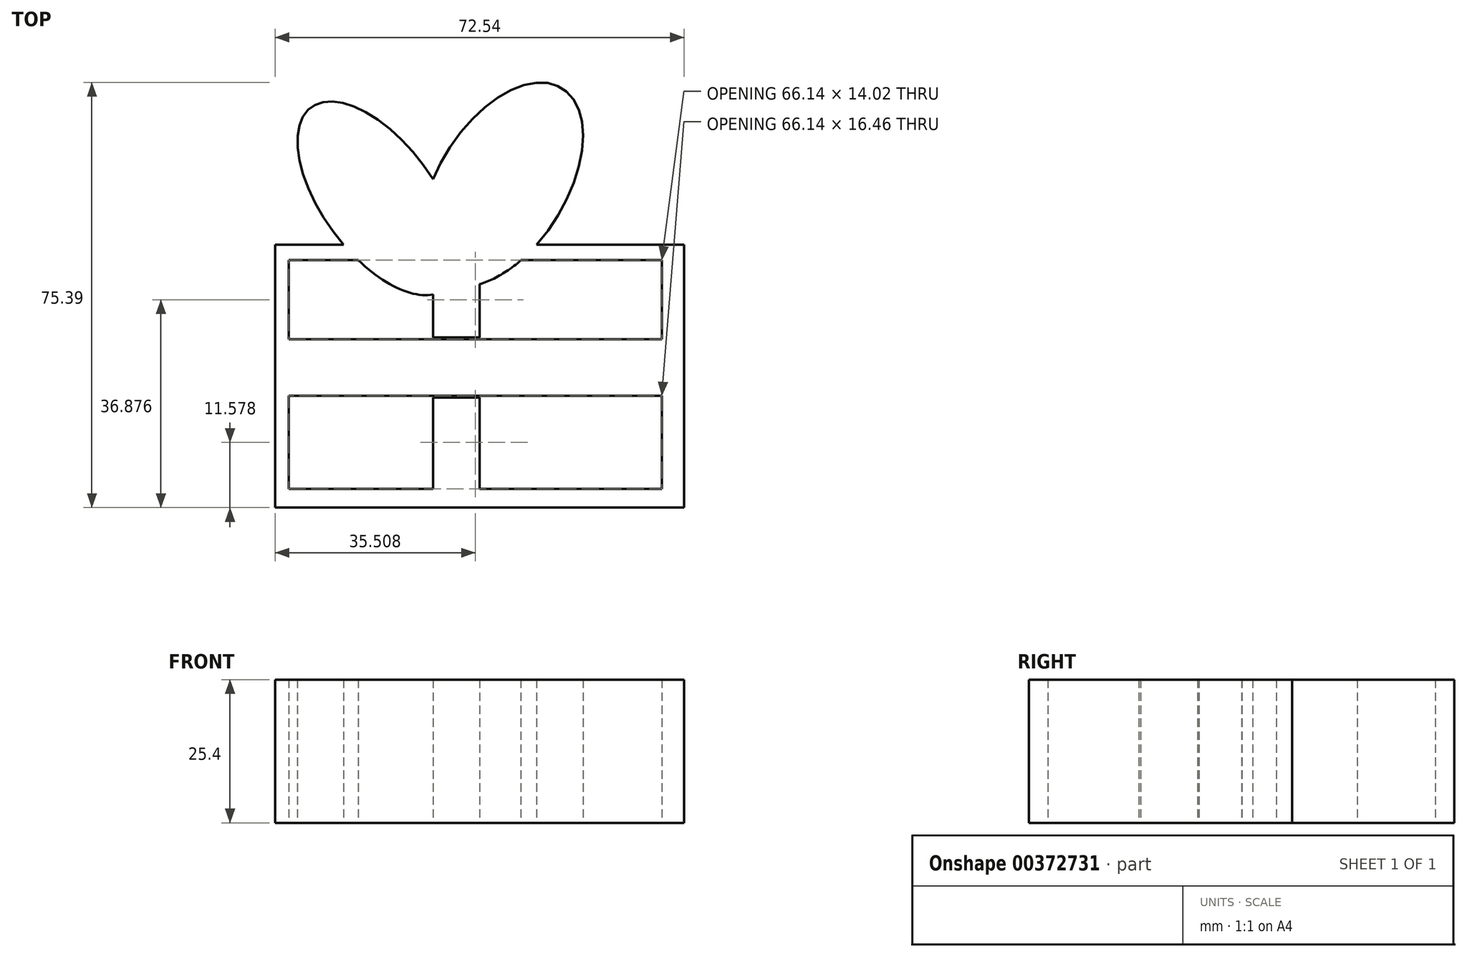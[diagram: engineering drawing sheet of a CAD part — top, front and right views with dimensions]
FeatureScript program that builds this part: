
annotation { "Feature Type Name" : "Feature", "Feature Type Description" : "" }
export const myFeature = defineFeature(function(context is Context, id is Id, definition is map)
    precondition{}
    {
        {
            var Q0;
            Q0=qCreatedBy(makeId("Top.planeOp"),FACE);
            var sketch = newSketch(context, id + "F0", { "sketchPlane" : qUnion([Q0])});
            skLineSegment(sketch, "E0.bottom", {"start": v(-28.04, 12.04) * mm, "end": v(44.5, 12.04) * mm});
            skLineSegment(sketch, "E0.top", {"start": v(-28.04, -34.6) * mm, "end": v(44.5, -34.6) * mm});
            skLineSegment(sketch, "E0.left", {"start": v(-28.04, 12.04) * mm, "end": v(-28.04, -34.6) * mm});
            skLineSegment(sketch, "E0.right", {"start": v(44.5, 12.04) * mm, "end": v(44.5, -34.6) * mm});
            skLineSegment(sketch, "E1.bottom", {"start": v(-25.6, 9.3) * mm, "end": v(40.54, 9.3) * mm});
            skLineSegment(sketch, "E1.top", {"start": v(-25.6, -31.24) * mm, "end": v(40.54, -31.24) * mm});
            skLineSegment(sketch, "E1.left", {"start": v(-25.6, 9.3) * mm, "end": v(-25.6, -31.24) * mm});
            skLineSegment(sketch, "E1.right", {"start": v(40.54, 9.3) * mm, "end": v(40.54, -31.24) * mm});
            skLineSegment(sketch, "E2.bottom", {"start": v(-25.6, -4.72) * mm, "end": v(44.5, -4.72) * mm});
            skLineSegment(sketch, "E2.top", {"start": v(-25.6, -4.42) * mm, "end": v(44.5, -4.42) * mm});
            skLineSegment(sketch, "E2.left", {"start": v(-28.04, -4.72) * mm, "end": v(-28.04, -4.42) * mm});
            skLineSegment(sketch, "E2.right", {"start": v(44.5, -4.72) * mm, "end": v(44.5, -4.42) * mm});
            skLineSegment(sketch, "E3.bottom", {"start": v(-25.6, -15.09) * mm, "end": v(44.5, -15.09) * mm});
            skLineSegment(sketch, "E3.top", {"start": v(-25.6, -14.78) * mm, "end": v(44.5, -14.78) * mm});
            skLineSegment(sketch, "E3.left", {"start": v(-25.6, -15.09) * mm, "end": v(-25.6, -14.78) * mm});
            skLineSegment(sketch, "E3.right", {"start": v(44.5, -15.09) * mm, "end": v(44.5, -14.78) * mm});
            skLineSegment(sketch, "E4", {"start": v(0, 9.3) * mm, "end": v(0, -31.24) * mm});
            skLineSegment(sketch, "E5", {"start": v(8.23, 9.3) * mm, "end": v(8.23, -31.24) * mm});
            skPoint(sketch, "E5.startSnap0", {"position": v(7.47, 9.3) * mm});
            skPoint(sketch, "E5.startSnap1", {"position": v(8.23, 12.04) * mm});
            skPoint(sketch, "E6.1.internal.orphan", {"position": v(0, 23.62) * mm});
            skEllipticalArc(sketch, "E7", {});
            skEllipticalArc(sketch, "E8.trimOffspring", {});
            const initialGuessF0  = {"E7": [-0.00975360069423914, 0.020269200205802917, 0.5926805994036081, -0.8054375873341025, 0.020056675187534876, 0.00993114980581942, 1.418696932754669, 0.12206321532883095], "E8.trimOffspring": [0.012191999703645706, 0.02270760014653206, -0.5299989795139679, -0.8479982793108444, 0.0201283427893708, 0.011335019917126201, 0.14448277518461064, 4.9992793105523]};
            skSetInitialGuess(sketch, initialGuessF0);
            skSolve(sketch);
        }
        {
            var Q0;
            Q0 = qSketchRegion(id + "F0", true);
            var Q1;
            {var subQ0=sQuery(id+"F0.wireOp",EDGE,"E2.bottom");var subQ1=sQuery(id+"F0.wireOp",EDGE,"E1.left");var subQ2=makeQuery(id+"F0.imprint","INTERSECT",VERTEX,{"derivedFrom":[subQ1,subQ0]});Q1=makeQuery(id+"F0.imprint","IMPRINT",FACE,{"disambiguationData":[TD([[makeQuery(id+"F0.imprint","IMPRINT",EDGE,{"disambiguationData":[TD([[subQ2,-1.0]])],"derivedFrom":subQ0}),-1.0]])]});}
            var Q2;
            {var subQ0=sQuery(id+"F0.wireOp",EDGE,"E4");var subQ1=sQuery(id+"F0.wireOp",EDGE,"E2.bottom");var subQ2=makeQuery(id+"F0.imprint","INTERSECT",VERTEX,{"derivedFrom":[subQ1,subQ0]});Q2=makeQuery(id+"F0.imprint","IMPRINT",FACE,{"disambiguationData":[TD([[makeQuery(id+"F0.imprint","IMPRINT",EDGE,{"disambiguationData":[TD([[subQ2,-1.0]])],"derivedFrom":subQ1}),-1.0]])]});}
            var Q3;
            {var subQ1=sQuery(id+"F0.wireOp",EDGE,"E2.top");var subQ5=sQuery(id+"F0.wireOp",EDGE,"E4");var subQ6=makeQuery(id+"F0.imprint","INTERSECT",VERTEX,{"derivedFrom":[subQ1,subQ5]});Q3=makeQuery(id+"F0.imprint","IMPRINT",FACE,{"disambiguationData":[TD([[makeQuery(id+"F0.imprint","IMPRINT",EDGE,{"disambiguationData":[TD([[subQ6,-1.0]])],"derivedFrom":subQ1}),1.0]])]});}
            var Q4;
            {var subQ1=sQuery(id+"F0.wireOp",EDGE,"E1.bottom");var subQ7=sQuery(id+"F0.wireOp",EDGE,"E4");var subQ9=makeQuery(id+"F0.imprint","INTERSECT",VERTEX,{"derivedFrom":[subQ1,subQ7]});Q4=makeQuery(id+"F0.imprint","IMPRINT",FACE,{"disambiguationData":[TD([[makeQuery(id+"F0.imprint","IMPRINT",EDGE,{"disambiguationData":[TD([[subQ9,-1.0]])],"derivedFrom":subQ1}),-1.0]])]});}
            var Q5;
            {var subQ0=sQuery(id+"F0.wireOp",EDGE,"E2.bottom");var subQ1=sQuery(id+"F0.wireOp",EDGE,"E1.right");var subQ2=makeQuery(id+"F0.imprint","INTERSECT",VERTEX,{"derivedFrom":[subQ1,subQ0]});Q5=makeQuery(id+"F0.imprint","IMPRINT",FACE,{"disambiguationData":[TD([[makeQuery(id+"F0.imprint","IMPRINT",EDGE,{"disambiguationData":[TD([[subQ2,-1.0]])],"derivedFrom":subQ1}),-1.0]])]});}
            var Q6;
            {var subQ0=sQuery(id+"F0.wireOp",EDGE,"E4");var subQ1=sQuery(id+"F0.wireOp",EDGE,"E1.top");var subQ2=makeQuery(id+"F0.imprint","INTERSECT",VERTEX,{"derivedFrom":[subQ1,subQ0]});Q6=makeQuery(id+"F0.imprint","IMPRINT",FACE,{"disambiguationData":[TD([[makeQuery(id+"F0.imprint","IMPRINT",EDGE,{"disambiguationData":[TD([[subQ2,-1.0]])],"derivedFrom":subQ1}),1.0]])]});}
            var Q7;
            {var subQ0=sQuery(id+"F0.wireOp",EDGE,"E4");var subQ1=sQuery(id+"F0.wireOp",EDGE,"E1.bottom");var subQ2=makeQuery(id+"F0.imprint","INTERSECT",VERTEX,{"derivedFrom":[subQ1,subQ0]});Q7=makeQuery(id+"F0.imprint","IMPRINT",FACE,{"disambiguationData":[TD([[makeQuery(id+"F0.imprint","IMPRINT",EDGE,{"disambiguationData":[TD([[subQ2,1.0]])],"derivedFrom":subQ1}),-1.0]])]});}
            var Q8;
            {var subQ0=sQuery(id+"F0.wireOp",EDGE,"E5");var subQ1=sQuery(id+"F0.wireOp",EDGE,"E1.bottom");var subQ2=makeQuery(id+"F0.imprint","INTERSECT",VERTEX,{"derivedFrom":[subQ1,subQ0]});Q8=makeQuery(id+"F0.imprint","IMPRINT",FACE,{"disambiguationData":[TD([[makeQuery(id+"F0.imprint","IMPRINT",EDGE,{"disambiguationData":[TD([[subQ2,-1.0]])],"derivedFrom":subQ1}),-1.0]])]});}
            extrude(context, id + "F1", {"entities" : qUnion([Q0, Q1, Q2, Q3, Q4, Q5, Q6, Q7, Q8]), "depth" : 25.4 * mm});
        }
    });
